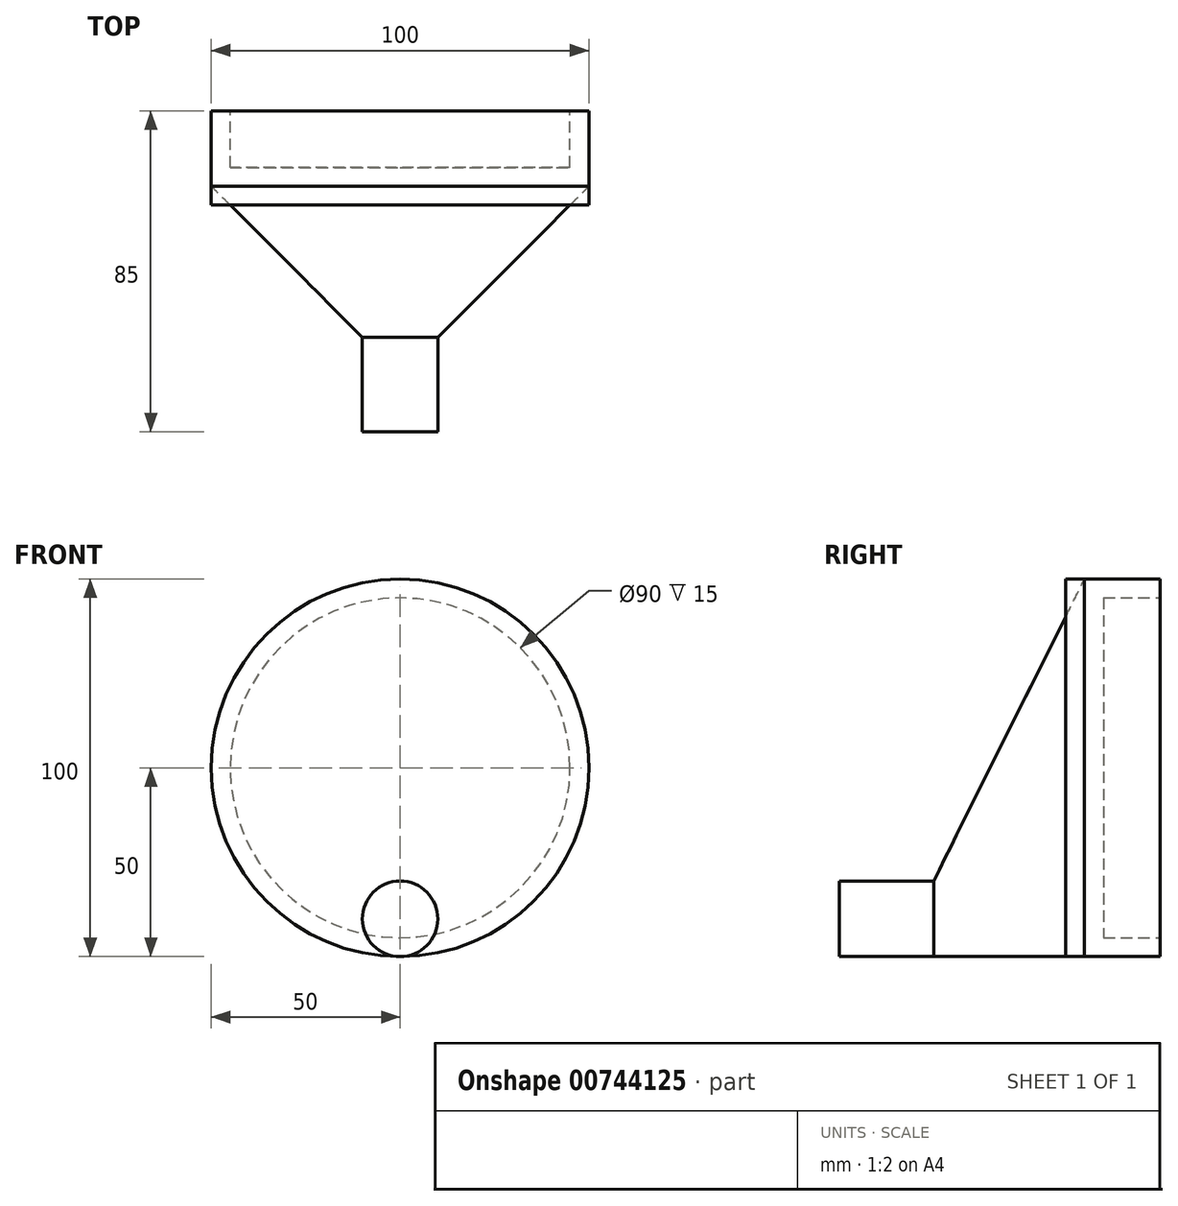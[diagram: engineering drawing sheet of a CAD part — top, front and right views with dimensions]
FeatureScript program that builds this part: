
annotation { "Feature Type Name" : "Feature", "Feature Type Description" : "" }
export const myFeature = defineFeature(function(context is Context, id is Id, definition is map)
    precondition{}
    {
        {
            var Q0;
            Q0=qCreatedBy(makeId("Front.planeOp"),FACE);
            var sketch = newSketch(context, id + "F0", { "sketchPlane" : qUnion([Q0])});
            skCircle(sketch, "E0", {"center": v(0, 0) * mm, "radius": 10 * mm});
            skSolve(sketch);
        }
        {
            var Q0;
            Q0=makeQuery(id+"F0.imprint","IMPRINT",FACE,{"disambiguationData":[TD([[makeQuery(id+"F0.imprint","IMPRINT",EDGE,{"derivedFrom":sQuery(id+"F0.wireOp",EDGE,"E0")}),1.0]])]});
            extrude(context, id + "F1", {"entities" : qUnion([Q0]), "depth" : 25 * mm, "offsetDistance" : 25 * mm});
        }
        {
            var Q0;
            Q0=qCreatedBy(makeId("Front.planeOp"),FACE);
            cPlane(context, id + "F2", {"entities" : qUnion([Q0]), "cplaneType" : CPlaneType.OFFSET, "offset" : 40 * mm, "oppositeDirection" : true, "width" : 150 * mm, "height" : 150 * mm});
        }
        {
            var Q0;
            Q0=qCreatedBy(id+"F2.planeOp",FACE);
            var sketch = newSketch(context, id + "F3", { "sketchPlane" : qUnion([Q0])});
            skCircle(sketch, "E1", {"center": v(0, 40) * mm, "radius": 50 * mm});
            skSolve(sketch);
        }
        {
            var Q1;
            Q1=makeQuery(id+"F3.imprint","IMPRINT",FACE,{"disambiguationData":[TD([[makeQuery(id+"F3.imprint","IMPRINT",EDGE,{"derivedFrom":sQuery(id+"F3.wireOp",EDGE,"E1")}),1.0]])]});
            var Q2;
            Q2=makeQuery(id+"F0.imprint","IMPRINT",FACE,{"disambiguationData":[TD([[makeQuery(id+"F0.imprint","IMPRINT",EDGE,{"derivedFrom":sQuery(id+"F0.wireOp",EDGE,"E0")}),1.0]])]});
            var Q3;
            Q3=sQuery(id+"F3.wireOp",EDGE,"E1");
            var Q4;
            Q4=sQuery(id+"F0.wireOp",EDGE,"E0");
            loft(context, id + "F4", {"operationType" : NewBodyOperationType.ADD, "sheetProfilesArray" : [{ "sheetProfileEntities" : qUnion([Q1]) }, { "sheetProfileEntities" : qUnion([Q2]) }], "wireProfilesArray" : [{ "wireProfileEntities" : qUnion([Q3]) }, { "wireProfileEntities" : qUnion([Q4]) }]});
        }
        {
            var Q0;
            Q0=makeQuery(id+"F4.opLoft","CAP_FACE",FACE,{"disambiguationData":[OSD([makeQuery(id+"F3.imprint","IMPRINT",FACE,{"disambiguationData":[TD([[makeQuery(id+"F3.imprint","IMPRINT",EDGE,{"derivedFrom":sQuery(id+"F3.wireOp",EDGE,"E1")}),1.0]])]})])],"isStart":true});
            extrude(context, id + "F5", {"entities" : qUnion([Q0]), "operationType" : NewBodyOperationType.ADD, "depth" : 20 * mm, "offsetDistance" : 25 * mm});
        }
        {
            var Q0;
            Q0=makeQuery(id+"F5.opExtrude","CAP_FACE",FACE,{"disambiguationData":[OSD([makeQuery(id+"F3.imprint","IMPRINT",FACE,{"disambiguationData":[TD([[makeQuery(id+"F3.imprint","IMPRINT",EDGE,{"derivedFrom":sQuery(id+"F3.wireOp",EDGE,"E1")}),1.0]])]})])],"isStart":false});
            var sketch = newSketch(context, id + "F6", { "sketchPlane" : qUnion([Q0])});
            skCircle(sketch, "E2", {"center": v(0, 40) * mm, "radius": 45 * mm});
            skSolve(sketch);
        }
        {
            var Q0;
            Q0=makeQuery(id+"F6.imprint","IMPRINT",FACE,{"disambiguationData":[TD([[makeQuery(id+"F6.imprint","IMPRINT",EDGE,{"derivedFrom":sQuery(id+"F6.wireOp",EDGE,"E2")}),1.0]])]});
            extrude(context, id + "F7", {"entities" : qUnion([Q0]), "operationType" : NewBodyOperationType.REMOVE, "oppositeDirection" : true, "depth" : 15 * mm, "offsetDistance" : 25 * mm});
        }
        {
            var Q0;
            Q0 = qSketchRegion(id + "F3", true);
            extrude(context, id + "F8", {"entities" : qUnion([Q0]), "depth" : 5 * mm, "offsetDistance" : 25 * mm});
        }
    });
